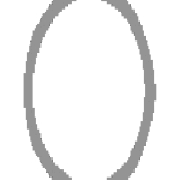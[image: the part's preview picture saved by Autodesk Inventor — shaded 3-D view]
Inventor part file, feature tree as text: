
AUTODESK INVENTOR PART (.ipt)
format: ipt  version: 2021 (Build 250183000, 183)  size: 134,144 bytes
history: native  units: in
note: dims shown in document units (in); Inventor stores cm internally (conversion verified against a paired STEP export)
features: plane x6, split x5, other x4, sketch x3
ambient origin geometry x8: Origin, YZ Plane, XZ Plane, XY Plane, X Axis, Y Axis, Z Axis, Center Point
bodies: Solid1 (feature_tree), Body (feature_tree)
feature tree (18):
  other  "Driven Length"
  other  "Frame Generator"
  other  "Start Plane"
  other  "End Plane"
  plane  "Work Plane5"
  split  "Split1"
  plane  "Work Plane6"
  split  "Split2"
  plane  "Work Plane7"
  split  "Split3"
  plane  "Work Plane8"
  split  "Split4"
  plane  "Work Plane9"
  split  "Split5"
  sketch  "Sketch"  dims[d2=20.0in d4=-0.1427in d5=20.0in d6=0.12in d7=0.0in d10=90.0deg d9=20.1427in]
  sketch  "Sketch4"  dims[d0=1.0in]
  plane  "Work Plane4"
  sketch  "Sketch5"  dims[d1=0.065in]
